FREECAD ASSEMBLY — COMPONENT RECIPES ("assemblies")

This assembly document has 3 components, labeled P0..P2 below (a component is one placed body or linked part). 1 of them carries a construction recipe — the FreeCAD feature program that regenerates the part from scratch, quoted from this document or its linked companion documents; the rest are supplied as boundary geometry only. No exploded tour is included for this assembly.
COMPONENT P0 — geometry summary ("Joystick v6"; no construction recipe available for this part):
  bounding box: 33.2 x 26.8 x 24.7 mm
  tessellated surface: 37,240 triangles
  volume: 4886 mm^3 (22% of its bounding box)
COMPONENT P1 — geometry summary ("left"; no construction recipe available for this part):
  bounding box: 126.7 x 48.0 x 12.9 mm
  tessellated surface: 125,918 triangles
  volume: 8489 mm^3 (11% of its bounding box)
COMPONENT P2 — recipe-attached ("thumbstick-breakout", a linked part whose construction recipe lives in a companion FreeCAD document of the same project; that document's serialized recipe follows).
Construction recipe (the companion document, serialized — sketch geometry with constraints, then the solid features built on it; lengths are millimeters unless a unit is written):

FCSTD DOCUMENT  (FreeCAD 1.0RUnknown)
Label: thumbstick-breakout
License: All rights reserved
LicenseURL: https://en.wikipedia.org/wiki/All_rights_reserved
objects: Sketcher::SketchObject×14, App::Part×6, PartDesign::Pad×6, PartDesign::ShapeBinder×5, PartDesign::Pocket×5, PartDesign::Body×4, Part::Feature×3, PartDesign::Thickness×2, PartDesign::CoordinateSystem×1, Part::Ellipsoid×1, PartDesign::Plane×1, PartDesign::Chamfer×1, PartDesign::Revolution×1
note: 88 computed .brp shape members not serialized (recipe doc carries the construction recipe); baked Part::Feature solids carry a one-line shape summary decoded from their .brp

FEATURE [PartDesign::CoordinateSystem] Local_CS_bbd4
  AttacherType = Attacher::AttachEngine3D
  MapMode = 2
FEATURE [Part::Feature] Pcb_bbd4
  Placement = pos=(-137.3,117.78,0) rot=(0,0,1;0rad)
  shape: bbox 25.4 x 31.75 x 1.6 mm, 24 faces (baked)
FEATURE [Sketcher::SketchObject] PCB_Sketch_bbd4
  ArcFitTolerance = 1e-06
  FullyConstrained = false
  MakeInternals = false
  sketch-geometry (4):
    g0: LineSegment StartX=0 StartY=31.75 StartZ=0 EndX=0 EndY=0 EndZ=0
    g1: LineSegment StartX=25.4 StartY=31.75 StartZ=0 EndX=0 EndY=31.75 EndZ=0
    g2: LineSegment StartX=0 StartY=0 StartZ=0 EndX=25.4 EndY=0 EndZ=0
    g3: LineSegment StartX=25.4 StartY=0 StartZ=0 EndX=25.4 EndY=31.75 EndZ=0
  constraints (4):
    c: Coincident(g0,g2)
    c: Coincident(g0,g1)
    c: Coincident(g2,g3)
    c: Coincident(g1,g3)
FEATURE [App::Part] Board_Geoms_bbd4
  Group = -> [Pcb_bbd4,PCB_Sketch_bbd4]
  Origin = -> Origin
FEATURE [Part::Feature] Shape  label="J1_SOLID_4955641dfa02"
  Placement = pos=(12.66,29.4,0) rot=(0,0.707107,0.707107;3.14159rad)
  shape: bbox 4.001 x 3.601 x 0.9007 mm, 670 faces (baked)
FEATURE [App::Part] Top_bbd4
  Group = -> [Shape]
  Origin = -> Origin003
FEATURE [App::Part] Step_Models_bbd4
  Group = -> [Top_bbd4]
  Origin = -> Origin002
FEATURE [App::Part] Board_bbd4  label="thumbstick-breakout"
  Group = -> [Local_CS_bbd4,Board_Geoms_bbd4,Step_Models_bbd4]
  Origin = -> Origin001
FEATURE [Sketcher::SketchObject] Sketch009  label="2.005"
  ArcFitTolerance = 1e-06
  FullyConstrained = false
  MakeInternals = false
  sketch-geometry (8):
    g0: LineSegment StartX=-2.4 StartY=31.75 StartZ=0 EndX=-2.4 EndY=0 EndZ=0
    g1: ArcOfCircle CenterX=4.026e-13 CenterY=0 CenterZ=0 NormalX=0 NormalY=0 NormalZ=1 AngleXU=0 Radius=2.4 StartAngle=3.14159 EndAngle=4.71239
    g2: LineSegment StartX=4.70767e-08 StartY=-2.4 StartZ=0 EndX=25.4 EndY=-2.4 EndZ=0
    g3: ArcOfCircle CenterX=25.4 CenterY=0 CenterZ=0 NormalX=0 NormalY=0 NormalZ=1 AngleXU=0 Radius=2.4 StartAngle=4.71239 EndAngle=6.28318
    g4: LineSegment StartX=27.8 StartY=-7.37231e-07 StartZ=0 EndX=27.8 EndY=31.75 EndZ=0
    g5: ArcOfCircle CenterX=25.4 CenterY=31.75 CenterZ=0 NormalX=0 NormalY=0 NormalZ=1 AngleXU=0 Radius=2.4 StartAngle=0 EndAngle=1.5708
    g6: LineSegment StartX=25.4 StartY=34.15 StartZ=0 EndX=7.84308e-07 EndY=34.15 EndZ=0
    g7: ArcOfCircle CenterX=0 CenterY=31.75 CenterZ=0 NormalX=0 NormalY=0 NormalZ=1 AngleXU=0 Radius=2.4 StartAngle=1.5708 EndAngle=3.14159
  constraints (12):
    c: Vertical(g0)
    c: Coincident(g0,g1)
    c: Coincident(g1,g2)
    c: Horizontal(g2)
    c: Coincident(g2,g3)
    c: Coincident(g3,g4)
    c: Vertical(g4)
    c: Coincident(g4,g5)
    c: Coincident(g5,g6)
    c: Horizontal(g6)
    c: Coincident(g6,g7)
    c: Coincident(g7,g0)
FEATURE [PartDesign::Pad] Pad
  Direction = (0,0,1)
  Length = 3.2
  Length2 = 10
  Profile = -> Sketch009
  ReferenceAxis = -> Sketch009 [N_Axis]
  Refine = true
  Suppressed = false
  Type = 0
FEATURE [PartDesign::Thickness] Thickness001
  Base = -> Pad [Face10]
  BaseFeature = -> Pad
  Intersection = false
  Join = 0
  Mode = 0
  Refine = true
  Reversed = true
  SupportTransform = false
  Suppressed = false
  Value = 2
FEATURE [PartDesign::ShapeBinder] ShapeBinder
  Support = -> [Pcb_bbd4]
  TraceSupport = false
FEATURE [Sketcher::SketchObject] Sketch010
  ArcFitTolerance = 1e-06
  AttachmentSupport = -> [Thickness001]
  ExternalGeometry = -> [ShapeBinder]
  FullyConstrained = true
  MakeInternals = false
  MapMode = 5
  Placement = pos=(0,0,2) rot=(0,0,1;0rad)
  sketch-geometry (4):
    g0: Circle CenterX=2.54 CenterY=29.21 CenterZ=0 NormalX=0 NormalY=0 NormalZ=1 AngleXU=0 Radius=1.25
    g1: Circle CenterX=22.86 CenterY=29.21 CenterZ=0 NormalX=0 NormalY=0 NormalZ=1 AngleXU=0 Radius=1.25
    g2: Circle CenterX=22.86 CenterY=2.54 CenterZ=0 NormalX=0 NormalY=0 NormalZ=1 AngleXU=0 Radius=1.25
    g3: Circle CenterX=2.54 CenterY=2.54 CenterZ=0 NormalX=0 NormalY=0 NormalZ=1 AngleXU=0 Radius=1.25
  constraints (8):
    c: Diameter(g0) = 2.5
    c: Coincident(g0,g-3)
    c: Diameter(g1) = 2.5
    c: Coincident(g1,g-4)
    c: Diameter(g2) = 2.5
    c: Coincident(g2,g-5)
    c: Diameter(g3) = 2.5
    c: Coincident(g3,g-6)
FEATURE [PartDesign::Pocket] Pocket002
  BaseFeature = -> Thickness001
  Direction = (0,0,-1)
  Length = 5
  Length2 = 5
  Profile = -> Sketch010
  ReferenceAxis = -> Sketch010 [N_Axis]
  Refine = true
  Suppressed = false
  Type = 1
FEATURE [PartDesign::ShapeBinder] ShapeBinder003
  Support = -> [Pcb_bbd4]
  TraceSupport = false
FEATURE [Sketcher::SketchObject] Sketch011
  ArcFitTolerance = 1e-06
  AttachmentSupport = -> [Pocket002]
  ExternalGeometry = -> [ShapeBinder003]
  FullyConstrained = true
  MakeInternals = false
  MapMode = 5
  Placement = pos=(0,0,2) rot=(0,0,1;0rad)
  sketch-geometry (14):
    g0: Circle CenterX=9.45 CenterY=24.043 CenterZ=0 NormalX=0 NormalY=0 NormalZ=1 AngleXU=0 Radius=1.5
    g1: Circle CenterX=15.95 CenterY=24.043 CenterZ=0 NormalX=0 NormalY=0 NormalZ=1 AngleXU=0 Radius=1.5
    g2: Circle CenterX=15.95 CenterY=19.543 CenterZ=0 NormalX=0 NormalY=0 NormalZ=1 AngleXU=0 Radius=1.5
    g3: Circle CenterX=19.025 CenterY=18.793 CenterZ=0 NormalX=0 NormalY=0 NormalZ=1 AngleXU=0 Radius=1.5
    g4: Circle CenterX=19.025 CenterY=8.793 CenterZ=0 NormalX=0 NormalY=0 NormalZ=1 AngleXU=0 Radius=1.5
    g5: Circle CenterX=9.45 CenterY=19.543 CenterZ=0 NormalX=0 NormalY=0 NormalZ=1 AngleXU=0 Radius=1.5
    g6: Circle CenterX=6.375 CenterY=18.793 CenterZ=0 NormalX=0 NormalY=0 NormalZ=1 AngleXU=0 Radius=1.5
    g7: Circle CenterX=6.375 CenterY=8.793 CenterZ=0 NormalX=0 NormalY=0 NormalZ=1 AngleXU=0 Radius=1.5
    g8: Circle CenterX=3.97 CenterY=16.293 CenterZ=0 NormalX=0 NormalY=0 NormalZ=1 AngleXU=0 Radius=1.2
    g9: Circle CenterX=3.97 CenterY=13.793 CenterZ=0 NormalX=0 NormalY=0 NormalZ=1 AngleXU=0 Radius=1.2
    g10: Circle CenterX=3.97 CenterY=11.293 CenterZ=0 NormalX=0 NormalY=0 NormalZ=1 AngleXU=0 Radius=1.2
    g11: Circle CenterX=10.2 CenterY=5.063 CenterZ=0 NormalX=0 NormalY=0 NormalZ=1 AngleXU=0 Radius=1.2
    g12: Circle CenterX=12.7 CenterY=5.063 CenterZ=0 NormalX=0 NormalY=0 NormalZ=1 AngleXU=0 Radius=1.2
    g13: Circle CenterX=15.2 CenterY=5.063 CenterZ=0 NormalX=0 NormalY=0 NormalZ=1 AngleXU=0 Radius=1.2
  constraints (28):
    c: Diameter(g0) = 3
    c: Coincident(g0,g-3)
    c: Diameter(g1) = 3
    c: Coincident(g1,g-5)
    c: Diameter(g2) = 3
    c: Coincident(g2,g-6)
    c: Diameter(g3) = 3
    c: Coincident(g3,g-12)
    c: Diameter(g4) = 3
    c: Coincident(g4,g-13)
    c: Diameter(g5) = 3
    c: Coincident(g5,g-4)
    c: Diameter(g6) = 3
    c: Coincident(g6,g-7)
    c: Diameter(g7) = 3
    c: Coincident(g7,g-11)
    c: Diameter(g8) = 2.4
    c: Coincident(g8,g-8)
    c: Diameter(g9) = 2.4
    c: Coincident(g9,g-9)
    c: Diameter(g10) = 2.4
    c: Coincident(g10,g-10)
    c: Diameter(g11) = 2.4
    c: Coincident(g11,g-16)
    c: Diameter(g12) = 2.4
    c: Coincident(g12,g-15)
    c: Diameter(g13) = 2.4
    c: Coincident(g13,g-14)
FEATURE [PartDesign::Pocket] Pocket003
  BaseFeature = -> Pocket002
  Direction = (0,0,-1)
  Length = 1
  Length2 = 5
  Profile = -> Sketch011
  ReferenceAxis = -> Sketch011 [N_Axis]
  Refine = true
  Suppressed = false
  Type = 0
FEATURE [PartDesign::Body] Body  label="base"
  AllowCompound = false
  Group = -> [Sketch009,Pad,Thickness001,ShapeBinder,Sketch010,Pocket002,ShapeBinder003,Sketch011,Pocket003]
  Origin = -> Origin010
  Placement = pos=(0,0,-3.6) rot=(0,0,1;0rad)
  Tip = -> Pocket003
FEATURE [PartDesign::ShapeBinder] ShapeBinder004
  Placement = pos=(-137.3,117.78,0) rot=(0,0,1;0rad)
  Support = -> [Pcb_bbd4]
  TraceSupport = false
FEATURE [Sketcher::SketchObject] Sketch012
  ArcFitTolerance = 1e-06
  AttachmentSupport = -> [ShapeBinder004]
  ExternalGeometry = -> [ShapeBinder004]
  FullyConstrained = false
  MakeInternals = false
  MapMode = 5
  Placement = pos=(-137.3,117.78,0) rot=(0,0,1;0rad)
  sketch-geometry (15):
    g0: Circle CenterX=146.75 CenterY=-93.737 CenterZ=0 NormalX=0 NormalY=0 NormalZ=1 AngleXU=0 Radius=0.2
    g1: Circle CenterX=153.25 CenterY=-93.737 CenterZ=0 NormalX=0 NormalY=0 NormalZ=1 AngleXU=0 Radius=0.2
    g2: Circle CenterX=153.25 CenterY=-98.237 CenterZ=0 NormalX=0 NormalY=0 NormalZ=1 AngleXU=0 Radius=0.2
    g3: Circle CenterX=156.325 CenterY=-98.987 CenterZ=0 NormalX=0 NormalY=0 NormalZ=1 AngleXU=0 Radius=0.2
    g4: Circle CenterX=146.75 CenterY=-98.237 CenterZ=0 NormalX=0 NormalY=0 NormalZ=1 AngleXU=0 Radius=0.2
    g5: Circle CenterX=143.675 CenterY=-98.987 CenterZ=0 NormalX=0 NormalY=0 NormalZ=1 AngleXU=0 Radius=0.2
    g6: Circle CenterX=141.27 CenterY=-101.487 CenterZ=0 NormalX=0 NormalY=0 NormalZ=1 AngleXU=0 Radius=0.2
    g7: Circle CenterX=141.27 CenterY=-103.987 CenterZ=0 NormalX=0 NormalY=0 NormalZ=1 AngleXU=0 Radius=0.2
    g8: Circle CenterX=141.27 CenterY=-106.487 CenterZ=0 NormalX=0 NormalY=0 NormalZ=1 AngleXU=0 Radius=0.2
    g9: Circle CenterX=143.675 CenterY=-108.987 CenterZ=0 NormalX=0 NormalY=0 NormalZ=1 AngleXU=0 Radius=0.2
    g10: Circle CenterX=147.5 CenterY=-112.717 CenterZ=0 NormalX=0 NormalY=0 NormalZ=1 AngleXU=0 Radius=0.2
    g11: Circle CenterX=150 CenterY=-112.717 CenterZ=0 NormalX=0 NormalY=0 NormalZ=1 AngleXU=0 Radius=0.2
    g12: Circle CenterX=152.5 CenterY=-112.717 CenterZ=0 NormalX=0 NormalY=0 NormalZ=1 AngleXU=0 Radius=0.2
    g13: Circle CenterX=152.599 CenterY=-112.925 CenterZ=0 NormalX=0 NormalY=0 NormalZ=1 AngleXU=0 Radius=0.2
    g14: Circle CenterX=156.325 CenterY=-108.987 CenterZ=0 NormalX=0 NormalY=0 NormalZ=1 AngleXU=0 Radius=0.2
  constraints (15):
    c: Coincident(g0,g-3)
    c: Coincident(g1,g-4)
    c: Coincident(g2,g-5)
    c: Coincident(g3,g-6)
    c: Coincident(g4,g-7)
    c: Coincident(g5,g-8)
    c: Coincident(g6,g-9)
    c: Coincident(g7,g-10)
    c: Coincident(g8,g-11)
    c: Coincident(g9,g-12)
    c: Coincident(g10,g-13)
    c: Coincident(g11,g-14)
    c: Coincident(g14,g-16)
    c: Equal(g0, g1-g14) x14
    c: Radius(g0) = 0.2
FEATURE [Sketcher::SketchObject] Sketch013
  ArcFitTolerance = 1e-06
  AttachmentSupport = -> [XY_Plane012]
  ExternalGeometry = -> [ShapeBinder004]
  FullyConstrained = false
  MakeInternals = false
  MapMode = 5
  sketch-geometry (14):
    g0: LineSegment StartX=17.3886 StartY=25.1014 StartZ=0 EndX=8.04245 EndY=25.1014 EndZ=0
    g1: LineSegment StartX=6.375 StartY=18.793 StartZ=0 EndX=2.6831 EndY=18.793 EndZ=0
    g2: LineSegment StartX=2.6831 StartY=18.793 StartZ=0 EndX=2.6831 EndY=8.793 EndZ=0
    g3: LineSegment StartX=2.6831 StartY=8.793 StartZ=0 EndX=6.375 EndY=8.793 EndZ=0
    g4: LineSegment StartX=8.26567 StartY=4.26908 StartZ=0 EndX=16.6861 EndY=4.26908 EndZ=0
    g5: LineSegment StartX=16.6861 StartY=4.26908 StartZ=0 EndX=16.6861 EndY=8.793 EndZ=0
    g6: LineSegment StartX=16.6861 StartY=8.793 StartZ=0 EndX=19.025 EndY=8.793 EndZ=0
    g7: LineSegment StartX=19.025 StartY=8.793 StartZ=0 EndX=19.025 EndY=18.793 EndZ=0
    g8: LineSegment StartX=19.025 StartY=18.793 StartZ=0 EndX=17.3886 EndY=18.793 EndZ=0
    g9: LineSegment StartX=17.3886 StartY=18.793 StartZ=0 EndX=17.3886 EndY=25.1014 EndZ=0
    g10: LineSegment StartX=6.375 StartY=18.793 StartZ=0 EndX=8.04245 EndY=18.793 EndZ=0
    g11: LineSegment StartX=8.04245 StartY=18.793 StartZ=0 EndX=8.04245 EndY=25.1014 EndZ=0
    g12: LineSegment StartX=6.375 StartY=8.793 StartZ=0 EndX=8.26567 EndY=8.793 EndZ=0
    g13: LineSegment StartX=8.26567 StartY=8.793 StartZ=0 EndX=8.26567 EndY=4.26908 EndZ=0
  constraints (30):
    c: Horizontal(g0)
    c: Horizontal(g1)
    c: Coincident(g1,g2)
    c: Vertical(g2)
    c: Coincident(g2,g3)
    c: Horizontal(g3)
    c: Horizontal(g4)
    c: Coincident(g4,g5)
    c: Vertical(g5)
    c: Coincident(g5,g6)
    c: Horizontal(g6)
    c: Coincident(g6,g7)
    c: Coincident(g7,g8)
    c: Horizontal(g8)
    c: Coincident(g8,g9)
    c: Coincident(g9,g0)
    c: Vertical(g9)
    c: Coincident(g7,g-8)
    c: Coincident(g6,g-9)
    c: Coincident(g3,g-10)
    c: Coincident(g1,g10)
    c: Horizontal(g10)
    c: Coincident(g10,g11)
    c: Coincident(g11,g0)
    c: Vertical(g11)
    c: Coincident(g3,g12)
    c: Horizontal(g12)
    c: Coincident(g12,g13)
    c: Coincident(g13,g4)
    c: Vertical(g13)
FEATURE [PartDesign::Pad] Pad001
  Direction = (0,0,1)
  Length = 9.3
  Length2 = 10
  Profile = -> Sketch013
  ReferenceAxis = -> Sketch013 [N_Axis]
  Refine = true
  Suppressed = false
  Type = 0
FEATURE [PartDesign::Pad] Pad002
  BaseFeature = -> Pad001
  Direction = (0,0,1)
  Length = 2
  Length2 = 10
  Profile = -> Sketch012
  ReferenceAxis = -> Sketch012 [N_Axis]
  Refine = true
  Reversed = true
  Suppressed = false
  Type = 0
FEATURE [PartDesign::Body] Body001  label="Body"
  AllowCompound = false
  Group = -> [ShapeBinder004,Sketch012,Sketch013,Pad001,Pad002]
  Origin = -> Origin012
  Tip = -> Pad002
FEATURE [Sketcher::SketchObject] Sketch014  label="2.4"
  ArcFitTolerance = 1e-06
  FullyConstrained = false
  MakeInternals = false
  sketch-geometry (8):
    g0: LineSegment StartX=-2.4 StartY=31.75 StartZ=0 EndX=-2.4 EndY=0 EndZ=0
    g1: ArcOfCircle CenterX=0 CenterY=0 CenterZ=0 NormalX=0 NormalY=0 NormalZ=1 AngleXU=0 Radius=2.4 StartAngle=3.14159 EndAngle=4.71239
    g2: LineSegment StartX=-4e-16 StartY=-2.4 StartZ=0 EndX=25.4 EndY=-2.4 EndZ=0
    g3: ArcOfCircle CenterX=25.4 CenterY=0 CenterZ=0 NormalX=0 NormalY=0 NormalZ=1 AngleXU=1.5708 Radius=2.4 StartAngle=3.14159 EndAngle=4.71239
    g4: LineSegment StartX=27.8 StartY=-4e-16 StartZ=0 EndX=27.8 EndY=31.75 EndZ=0
    g5: ArcOfCircle CenterX=25.4 CenterY=31.75 CenterZ=0 NormalX=0 NormalY=0 NormalZ=1 AngleXU=-3.14159 Radius=2.4 StartAngle=3.14159 EndAngle=4.71239
    g6: LineSegment StartX=25.4 StartY=34.15 StartZ=0 EndX=0 EndY=34.15 EndZ=0
    g7: ArcOfCircle CenterX=0 CenterY=31.75 CenterZ=0 NormalX=0 NormalY=0 NormalZ=1 AngleXU=-1.5708 Radius=2.4 StartAngle=3.14159 EndAngle=4.71239
  constraints (12):
    c: Vertical(g0)
    c: Coincident(g0,g1)
    c: Coincident(g1,g2)
    c: Horizontal(g2)
    c: Coincident(g2,g3)
    c: Coincident(g3,g4)
    c: Vertical(g4)
    c: Coincident(g4,g5)
    c: Coincident(g5,g6)
    c: Horizontal(g6)
    c: Coincident(g6,g7)
    c: Coincident(g7,g0)
FEATURE [PartDesign::ShapeBinder] ShapeBinder005
  Support = -> [Pcb_bbd4]
  TraceSupport = false
FEATURE [Sketcher::SketchObject] Sketch
  ArcFitTolerance = 1e-06
  AttachmentSupport = -> [XY_Plane013]
  ExternalGeometry = -> [ShapeBinder005]
  FullyConstrained = true
  MakeInternals = false
  MapMode = 5
  sketch-geometry (2):
    g0: LineSegment [constr] StartX=6.375 StartY=18.793 StartZ=0 EndX=19.025 EndY=8.793 EndZ=0
    g1: Circle CenterX=12.7 CenterY=13.793 CenterZ=0 NormalX=0 NormalY=0 NormalZ=1 AngleXU=0 Radius=2
  constraints (4):
    c: Coincident(g0,g-3)
    c: Coincident(g0,g-5)
    c: Symmetric(g0,g0,g1)
    c: Diameter(g1) = 4
FEATURE [PartDesign::Pad] Pad003
  Direction = (0,0,1)
  Length = 12
  Length2 = 10
  Profile = -> Sketch
  ReferenceAxis = -> Sketch [N_Axis]
  Refine = true
  Suppressed = false
  Type = 0
FEATURE [PartDesign::Body] Body002  label="stick"
  AllowCompound = false
  Group = -> [ShapeBinder005,Sketch,Pad003]
  Origin = -> Origin013
  Placement = pos=(0,0,6.5) rot=(0,0,1;0rad)
  Tip = -> Pad003
FEATURE [Part::Feature] Part__Feature001  label="Thumbstick"
  Placement = pos=(12.7,13.8,-2.8) rot=(0,0,1;0rad)
  shape: bbox 24.74 x 24.74 x 17.5 mm, 20 faces (baked)
FEATURE [App::Part] Part  label="thumbstick"
  Group = -> [Body001,Body002,Part__Feature001]
  Origin = -> Origin011
FEATURE [Sketcher::SketchObject] Sketch015  label="2.006"
  ArcFitTolerance = 1e-06
  FullyConstrained = false
  MakeInternals = false
  sketch-geometry (8):
    g0: LineSegment StartX=-2.4 StartY=31.75 StartZ=0 EndX=-2.4 EndY=0 EndZ=0
    g1: ArcOfCircle CenterX=0 CenterY=0 CenterZ=0 NormalX=0 NormalY=0 NormalZ=1 AngleXU=0 Radius=2.4 StartAngle=3.14159 EndAngle=4.71239
    g2: LineSegment StartX=-4e-16 StartY=-2.4 StartZ=0 EndX=25.4 EndY=-2.4 EndZ=0
    g3: ArcOfCircle CenterX=25.4 CenterY=0 CenterZ=0 NormalX=0 NormalY=0 NormalZ=1 AngleXU=1.5708 Radius=2.4 StartAngle=3.14159 EndAngle=4.71239
    g4: LineSegment StartX=27.8 StartY=-7e-16 StartZ=0 EndX=27.8 EndY=31.75 EndZ=0
    g5: ArcOfCircle CenterX=25.4 CenterY=31.75 CenterZ=0 NormalX=0 NormalY=0 NormalZ=1 AngleXU=-3.14159 Radius=2.4 StartAngle=3.14159 EndAngle=4.71239
    g6: LineSegment StartX=25.4 StartY=34.15 StartZ=0 EndX=0 EndY=34.15 EndZ=0
    g7: ArcOfCircle CenterX=0 CenterY=31.75 CenterZ=0 NormalX=0 NormalY=0 NormalZ=1 AngleXU=-1.5708 Radius=2.4 StartAngle=3.14159 EndAngle=4.71239
  constraints (12):
    c: Vertical(g0)
    c: Coincident(g0,g1)
    c: Coincident(g1,g2)
    c: Horizontal(g2)
    c: Coincident(g2,g3)
    c: Coincident(g3,g4)
    c: Vertical(g4)
    c: Coincident(g4,g5)
    c: Coincident(g5,g6)
    c: Horizontal(g6)
    c: Coincident(g6,g7)
    c: Coincident(g7,g0)
FEATURE [PartDesign::Pad] Pad004
  Direction = (0,0,1)
  Length = 5.3
  Length2 = 10
  Profile = -> Sketch015
  ReferenceAxis = -> Sketch015 [N_Axis]
  Refine = true
  Suppressed = false
  Type = 0
FEATURE [PartDesign::Thickness] Thickness
  Base = -> Pad004 [Face9]
  BaseFeature = -> Pad004
  Intersection = false
  Join = 0
  Mode = 0
  Refine = true
  Reversed = true
  SupportTransform = false
  Suppressed = false
  Value = 2
FEATURE [PartDesign::ShapeBinder] ShapeBinder006
  Support = -> [Pocket003]
  TraceSupport = false
FEATURE [Sketcher::SketchObject] Sketch016
  ArcFitTolerance = 1e-06
  AttachmentSupport = -> [Thickness]
  ExternalGeometry = -> [ShapeBinder006]
  FullyConstrained = true
  MakeInternals = false
  MapMode = 5
  Placement = pos=(0,0,0) rot=(1,0,0;3.14159rad)
  sketch-geometry (8):
    g0: Circle CenterX=2.54 CenterY=-2.54 CenterZ=0 NormalX=0 NormalY=0 NormalZ=1 AngleXU=0 Radius=3
    g1: Circle CenterX=22.86 CenterY=-2.54 CenterZ=0 NormalX=0 NormalY=0 NormalZ=1 AngleXU=0 Radius=3
    g2: Circle CenterX=22.86 CenterY=-29.21 CenterZ=0 NormalX=0 NormalY=0 NormalZ=1 AngleXU=0 Radius=3
    g3: Circle CenterX=2.54 CenterY=-29.21 CenterZ=0 NormalX=0 NormalY=0 NormalZ=1 AngleXU=0 Radius=3
    g4: Circle CenterX=2.54 CenterY=-2.54 CenterZ=0 NormalX=0 NormalY=0 NormalZ=1 AngleXU=0 Radius=1.65
    g5: Circle CenterX=22.86 CenterY=-2.54 CenterZ=0 NormalX=0 NormalY=0 NormalZ=1 AngleXU=0 Radius=1.65
    g6: Circle CenterX=22.86 CenterY=-29.21 CenterZ=0 NormalX=0 NormalY=0 NormalZ=1 AngleXU=0 Radius=1.65
    g7: Circle CenterX=2.54 CenterY=-29.21 CenterZ=0 NormalX=0 NormalY=0 NormalZ=1 AngleXU=0 Radius=1.65
  constraints (16):
    c: Diameter(g0) = 6
    c: Coincident(g0,g-3)
    c: Diameter(g1) = 6
    c: Coincident(g1,g-4)
    c: Diameter(g2) = 6
    c: Coincident(g2,g-5)
    c: Diameter(g3) = 6
    c: Coincident(g3,g-6)
    c: Diameter(g4) = 3.3
    c: Coincident(g4,g0)
    c: Diameter(g5) = 3.3
    c: Coincident(g5,g1)
    c: Diameter(g6) = 3.3
    c: Coincident(g6,g2)
    c: Diameter(g7) = 3.3
    c: Coincident(g7,g3)
FEATURE [Part::Ellipsoid] Ellipsoid
  Angle1 = -90
  Angle2 = 90
  Angle3 = 180
  AttacherType = Attacher::AttachEngine3D
  Placement = pos=(12.7,13.8,9.3) rot=(1,0,0;1.5708rad)
  Radius1 = 12.37
  Radius2 = 12.37
  Radius3 = 8
FEATURE [PartDesign::Plane] DatumPlane
  AttachmentOffset = pos=(0,0,12.7) rot=(0,0,1;0rad)
  AttachmentSupport = -> [YZ_Plane014]
  Length = 70.0266
  MapMode = 5
  Placement = pos=(12.7,0,0) rot=(0.57735,0.57735,0.57735;2.0944rad)
  ResizeMode = 0
  Width = 60.8766
FEATURE [Sketcher::SketchObject] Sketch017
  ArcFitTolerance = 1e-06
  AttachmentSupport = -> [DatumPlane]
  FullyConstrained = false
  MakeInternals = false
  MapMode = 5
  Placement = pos=(12.7,0,0) rot=(0.57735,0.57735,0.57735;2.0944rad)
  sketch-geometry (18):
    g0: Circle [constr] CenterX=29.1118 CenterY=3.8 CenterZ=0 NormalX=0 NormalY=0 NormalZ=1 AngleXU=0 Radius=1
    g1: Circle [constr] CenterX=30.0485 CenterY=13.7535 CenterZ=0 NormalX=0 NormalY=0 NormalZ=1 AngleXU=0 Radius=1
    g2: Circle [constr] CenterX=23.3909 CenterY=17.1877 CenterZ=0 NormalX=0 NormalY=0 NormalZ=1 AngleXU=0 Radius=1
    g3: BSplineCurve PolesCount=3 KnotsCount=2 Degree=2 IsPeriodic=0
    g4: GeomPoint [constr] X=29.1118 Y=3.8 Z=0
    g5: GeomPoint [constr] X=23.3909 Y=17.1877 Z=0
    g6: LineSegment StartX=23.3909 StartY=17.1877 StartZ=0 EndX=13.7824 EndY=17.1877 EndZ=0
    g7: Circle [constr] CenterX=28.1118 CenterY=3.8 CenterZ=0 NormalX=0 NormalY=0 NormalZ=1 AngleXU=0 Radius=1
    g8: Circle [constr] CenterX=28.4002 CenterY=12.6207 CenterZ=0 NormalX=0 NormalY=0 NormalZ=1 AngleXU=0 Radius=1
    g9: Circle [constr] CenterX=23.1917 CenterY=16.2077 CenterZ=0 NormalX=0 NormalY=0 NormalZ=1 AngleXU=0 Radius=1
    g10: BSplineCurve PolesCount=3 KnotsCount=2 Degree=2 IsPeriodic=0
    g11: GeomPoint [constr] X=28.1118 Y=3.8 Z=0
    g12: GeomPoint [constr] X=23.1917 Y=16.2077 Z=0
    g13: LineSegment StartX=28.1118 StartY=3.8 StartZ=0 EndX=29.1118 EndY=3.8 EndZ=0
    g14: LineSegment StartX=13.7824 StartY=17.1877 StartZ=0 EndX=13.7824 EndY=16.2077 EndZ=0
    g15: LineSegment StartX=13.7824 StartY=16.2077 StartZ=0 EndX=23.1917 EndY=16.2077 EndZ=0
    g16: LineSegment [constr] StartX=1.40969 StartY=9.23031 StartZ=0 EndX=26.155 EndY=9.23031 EndZ=0
    g17: LineSegment [constr] StartX=13.7824 StartY=9.23031 StartZ=0 EndX=13.7824 EndY=17.9973 EndZ=0
  constraints (33):
    c: Weight(g0) = 1
    c: Equal(g0,g1)
    c: Equal(g0,g2)
    c: InternalAlignment(g0,g3)
    c: InternalAlignment(g1,g3)
    c: InternalAlignment(g2,g3)
    c: InternalAlignment(g4,g3)
    c: InternalAlignment(g5,g3)
    c: Coincident(g6,g3)
    c: Horizontal(g6)
    c: Weight(g7) = 1
    c: Equal(g7,g8)
    c: Equal(g7,g9)
    c: InternalAlignment(g7,g10)
    c: InternalAlignment(g8,g10)
    c: InternalAlignment(g9,g10)
    c: InternalAlignment(g11,g10)
    c: InternalAlignment(g12,g10)
    c: Coincident(g13,g10)
    c: Coincident(g13,g3)
    c: Horizontal(g13)
    c: DistanceX(g13,g13) = 1
    c: Distance(g3,g10) = 1
    c: Distance(g1,g8) = 2
    c: Coincident(g6,g14)
    c: Vertical(g14)
    c: Coincident(g15,g10)
    c: Horizontal(g15)
    c: Horizontal(g16)
    c: Symmetric(g16,g16,g17)
    c: Vertical(g17)
    c: PointOnObject(g6,g17)
    c: Distance(g10,g-3) = 1.5
FEATURE [PartDesign::Chamfer] Chamfer
  Angle = 45
  Base = -> Thickness [Edge4]
  BaseFeature = -> Thickness
  ChamferType = 0
  FlipDirection = false
  Refine = true
  Size = 1.5
  Size2 = 1
  SupportTransform = false
  Suppressed = false
  UseAllEdges = false
FEATURE [PartDesign::Pad] Pad005
  BaseFeature = -> Chamfer
  Direction = (0,0,-1)
  Length = 3.3
  Length2 = 10
  Profile = -> Sketch016
  ReferenceAxis = -> Sketch016 [N_Axis]
  Refine = true
  Reversed = true
  Suppressed = false
  Type = 0
FEATURE [PartDesign::Revolution] Revolution
  Angle = 360
  Angle2 = 60
  Axis = (0,0,-1)
  Base = (12.7,13.7824,17.1877)
  BaseFeature = -> Pad005
  Profile = -> Sketch017
  ReferenceAxis = -> Sketch017 [Edge4]
  Refine = true
  Reversed = true
  Suppressed = false
  Type = 0
FEATURE [Sketcher::SketchObject] Sketch018
  ArcFitTolerance = 1e-06
  AttachmentSupport = -> [Revolution]
  ExternalGeometry = -> [Revolution]
  FullyConstrained = true
  MakeInternals = false
  MapMode = 5
  Placement = pos=(0,0,17.1877) rot=(0,0,1;0rad)
  sketch-geometry (1):
    g0: Circle CenterX=12.7 CenterY=13.7824 CenterZ=0 NormalX=0 NormalY=0 NormalZ=1 AngleXU=0 Radius=9.5
  constraints (2):
    c: Coincident(g0,g-3)
    c: Diameter(g0) = 19
FEATURE [PartDesign::Pocket] Pocket
  BaseFeature = -> Revolution
  Direction = (0,0,-1)
  Length = 14
  Length2 = 5
  Profile = -> Sketch018
  ReferenceAxis = -> Sketch018 [N_Axis]
  Refine = true
  Suppressed = false
  Type = 0
FEATURE [Sketcher::SketchObject] Sketch019
  ArcFitTolerance = 1e-06
  AttachmentSupport = -> [Pocket]
  FullyConstrained = true
  MakeInternals = false
  MapMode = 5
  Placement = pos=(0,0,5.3) rot=(0,0,1;0rad)
  sketch-geometry (1):
    g0: Circle CenterX=12.7 CenterY=13.7824 CenterZ=0 NormalX=0 NormalY=0 NormalZ=1 AngleXU=0 Radius=14.157
  constraints (2):
    c: Coincident(g0,g-3)
    c: Equal(g0,g-3)
FEATURE [PartDesign::Pocket] Pocket004
  BaseFeature = -> Pocket
  Direction = (0,0,-1)
  Length = 2
  Length2 = 5
  Profile = -> Sketch019
  ReferenceAxis = -> Sketch019 [N_Axis]
  Refine = true
  Suppressed = false
  Type = 0
FEATURE [Sketcher::SketchObject] Sketch020
  ArcFitTolerance = 1e-06
  AttachmentSupport = -> [Pocket004]
  ExternalGeometry = -> [Pocket004]
  FullyConstrained = false
  MakeInternals = false
  MapMode = 5
  Placement = pos=(0,34.15,0) rot=(0,0.707107,0.707107;3.14159rad)
  sketch-geometry (4):
    g0: LineSegment StartX=-15.1629 StartY=0 StartZ=0 EndX=-10.1629 EndY=0 EndZ=0
    g1: LineSegment StartX=-10.1629 StartY=0 StartZ=0 EndX=-10.1629 EndY=1.3 EndZ=0
    g2: LineSegment StartX=-10.1629 StartY=1.3 StartZ=0 EndX=-15.1629 EndY=1.3 EndZ=0
    g3: LineSegment StartX=-15.1629 StartY=1.3 StartZ=0 EndX=-15.1629 EndY=0 EndZ=0
  constraints (11):
    c: Coincident(g0,g1)
    c: Coincident(g1,g2)
    c: Coincident(g2,g3)
    c: Coincident(g3,g0)
    c: Horizontal(g0)
    c: Horizontal(g2)
    c: Vertical(g1)
    c: Vertical(g3)
    c: PointOnObject(g0,g-3)
    c: DistanceX(g2,g2) = 5
    c: DistanceY(g1,g1) = 1.3
FEATURE [PartDesign::Pocket] Pocket005
  BaseFeature = -> Pocket004
  Direction = (0,-1,2e-16)
  Length = 2
  Length2 = 5
  Profile = -> Sketch020
  ReferenceAxis = -> Sketch020 [N_Axis]
  Refine = true
  Suppressed = false
  Type = 0
FEATURE [PartDesign::Body] Body003  label="top"
  AllowCompound = false
  Group = -> [Sketch015,Pad004,Thickness,Chamfer,ShapeBinder006,Sketch016,Pad005,DatumPlane,Sketch017,Revolution,Sketch018,Pocket,Sketch019,Pocket004,Sketch020,Pocket005]
  Origin = -> Origin014
  Tip = -> Pocket005
FEATURE [App::Part] Part001  label="case"
  Group = -> [Body,Body003,Ellipsoid]
  Origin = -> Origin009
PROVENANCE & LICENSES
A FreeCAD (.FCStd) document from a public repository crawl; recipes are the document's own serialized feature recipes (and, for linked parts, companion documents' recipes).
License: gpl-3.0.
